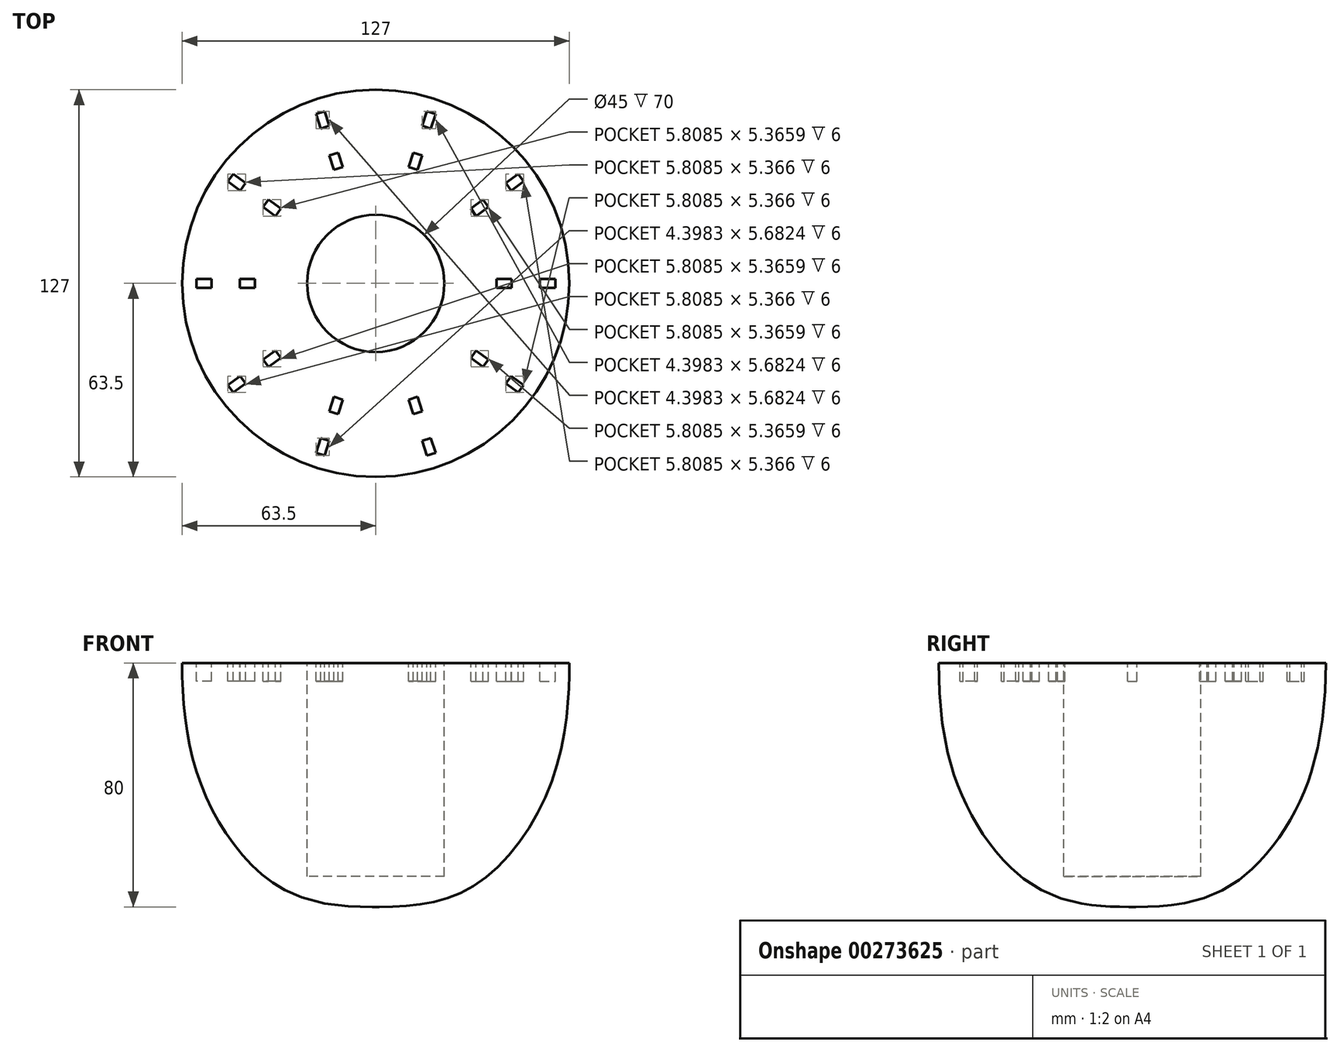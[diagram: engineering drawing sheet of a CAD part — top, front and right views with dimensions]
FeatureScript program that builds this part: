
annotation { "Feature Type Name" : "Feature", "Feature Type Description" : "" }
export const myFeature = defineFeature(function(context is Context, id is Id, definition is map)
    precondition{}
    {
        {
            var Q0;
            Q0=qCreatedBy(makeId("Front.planeOp"),FACE);
            var sketch = newSketch(context, id + "F0", { "sketchPlane" : qUnion([Q0])});
            skLineSegment(sketch, "E0", {"start": v(0, 0) * mm, "end": v(63.5, 0) * mm});
            skLineSegment(sketch, "E1", {"start": v(0, 0) * mm, "end": v(0, -80) * mm});
            skFitSpline(sketch, "E2", {"points": [v(0, -80) * mm, v(31.42, -73.58) * mm, v(58.27, -37.26) * mm, v(63.5, 0) * mm], "startDerivative": vector(100.46, -0.55) * mm, "endDerivative": vector(0, 86.8) * mm});
            skSolve(sketch);
        }
        {
            var Q0;
            Q0 = qSketchRegion(id + "F0", true);
            var Q1;
            Q1=sQuery(id+"F0.wireOp",EDGE,"E1");
            revolve(context, id + "F1", {"entities" : qUnion([Q0]), "axis" : qUnion([Q1]), "revolveType" : RevolveType.FULL});
        }
        {
            var Q0;
            Q0=makeQuery(id+"F1.opRevolve","SWEPT_FACE",FACE,{"disambiguationData":[OSD([sQuery(id+"F0.wireOp",EDGE,"E0")])]});
            var sketch = newSketch(context, id + "F2", { "sketchPlane" : qUnion([Q0])});
            skCircle(sketch, "E3", {"center": v(0, 0) * mm, "radius": 22.5 * mm});
            skSolve(sketch);
        }
        {
            var Q0;
            Q0=makeQuery(id+"F2.imprint","IMPRINT",FACE,{"disambiguationData":[TD([[makeQuery(id+"F2.imprint","IMPRINT",EDGE,{"derivedFrom":sQuery(id+"F2.wireOp",EDGE,"E3")}),1.0]])]});
            extrude(context, id + "F3", {"entities" : qUnion([Q0]), "operationType" : NewBodyOperationType.REMOVE, "oppositeDirection" : true, "depth" : 70 * mm});
        }
        {
            var Q0;
            Q0=qCreatedBy(makeId("Top.planeOp"),FACE);
            var sketch = newSketch(context, id + "F4", { "sketchPlane" : qUnion([Q0])});
            skLineSegment(sketch, "E4.bottom", {"start": v(-39.63, -1.5) * mm, "end": v(-44.63, -1.5) * mm});
            skLineSegment(sketch, "E4.top", {"start": v(-39.63, 1.5) * mm, "end": v(-44.63, 1.5) * mm});
            skLineSegment(sketch, "E4.left", {"start": v(-39.63, -1.5) * mm, "end": v(-39.63, 1.5) * mm});
            skLineSegment(sketch, "E4.right", {"start": v(-44.63, -1.5) * mm, "end": v(-44.63, 1.5) * mm});
            skPoint(sketch, "E4.middle", {"position": v(-42.12, 0) * mm});
            skLineSegment(sketch, "E5.bottom", {"start": v(-53.88, 1.5) * mm, "end": v(-58.88, 1.5) * mm});
            skLineSegment(sketch, "E5.top", {"start": v(-53.88, -1.5) * mm, "end": v(-58.88, -1.5) * mm});
            skLineSegment(sketch, "E5.left", {"start": v(-53.88, 1.5) * mm, "end": v(-53.88, -1.5) * mm});
            skLineSegment(sketch, "E5.right", {"start": v(-58.88, 1.5) * mm, "end": v(-58.88, -1.5) * mm});
            skPoint(sketch, "E5.middle", {"position": v(-56.38, 0) * mm});
            skPoint(sketch, "E6.1.0", {"position": v(-34.08, -24.76) * mm});
            skPoint(sketch, "E6.1.1", {"position": v(-45.6, -33.14) * mm});
            skLineSegment(sketch, "E6.1.2", {"start": v(-42.7, -32.88) * mm, "end": v(-46.75, -35.82) * mm});
            skLineSegment(sketch, "E6.1.3", {"start": v(-44.47, -30.45) * mm, "end": v(-48.51, -33.4) * mm});
            skLineSegment(sketch, "E6.1.4", {"start": v(-32.94, -22.08) * mm, "end": v(-36.98, -25.02) * mm});
            skLineSegment(sketch, "E6.1.5", {"start": v(-31.18, -24.5) * mm, "end": v(-35.22, -27.44) * mm});
            skLineSegment(sketch, "E6.1.6", {"start": v(-44.47, -30.45) * mm, "end": v(-42.7, -32.88) * mm});
            skLineSegment(sketch, "E6.1.7", {"start": v(-35.22, -27.44) * mm, "end": v(-36.98, -25.02) * mm});
            skLineSegment(sketch, "E6.1.8", {"start": v(-31.18, -24.5) * mm, "end": v(-32.94, -22.08) * mm});
            skLineSegment(sketch, "E6.1.9", {"start": v(-48.51, -33.4) * mm, "end": v(-46.75, -35.82) * mm});
            skPoint(sketch, "E6.2.0", {"position": v(-13.02, -40.06) * mm});
            skPoint(sketch, "E6.2.1", {"position": v(-17.42, -53.62) * mm});
            skLineSegment(sketch, "E6.2.2", {"start": v(-15.22, -51.7) * mm, "end": v(-16.77, -56.46) * mm});
            skLineSegment(sketch, "E6.2.3", {"start": v(-18.07, -50.77) * mm, "end": v(-19.62, -55.53) * mm});
            skLineSegment(sketch, "E6.2.4", {"start": v(-13.67, -37.22) * mm, "end": v(-15.22, -41.98) * mm});
            skLineSegment(sketch, "E6.2.5", {"start": v(-10.82, -38.15) * mm, "end": v(-12.36, -42.9) * mm});
            skLineSegment(sketch, "E6.2.6", {"start": v(-18.07, -50.77) * mm, "end": v(-15.22, -51.7) * mm});
            skLineSegment(sketch, "E6.2.7", {"start": v(-12.36, -42.9) * mm, "end": v(-15.22, -41.98) * mm});
            skLineSegment(sketch, "E6.2.8", {"start": v(-10.82, -38.15) * mm, "end": v(-13.67, -37.22) * mm});
            skLineSegment(sketch, "E6.2.9", {"start": v(-19.62, -55.53) * mm, "end": v(-16.77, -56.46) * mm});
            skPoint(sketch, "E6.3.0", {"position": v(13.02, -40.06) * mm});
            skPoint(sketch, "E6.3.1", {"position": v(17.42, -53.62) * mm});
            skLineSegment(sketch, "E6.3.2", {"start": v(18.07, -50.77) * mm, "end": v(19.62, -55.53) * mm});
            skLineSegment(sketch, "E6.3.3", {"start": v(15.22, -51.7) * mm, "end": v(16.77, -56.46) * mm});
            skLineSegment(sketch, "E6.3.4", {"start": v(10.82, -38.15) * mm, "end": v(12.36, -42.9) * mm});
            skLineSegment(sketch, "E6.3.5", {"start": v(13.67, -37.22) * mm, "end": v(15.22, -41.98) * mm});
            skLineSegment(sketch, "E6.3.6", {"start": v(15.22, -51.7) * mm, "end": v(18.07, -50.77) * mm});
            skLineSegment(sketch, "E6.3.7", {"start": v(15.22, -41.98) * mm, "end": v(12.36, -42.9) * mm});
            skLineSegment(sketch, "E6.3.8", {"start": v(13.67, -37.22) * mm, "end": v(10.82, -38.15) * mm});
            skLineSegment(sketch, "E6.3.9", {"start": v(16.77, -56.46) * mm, "end": v(19.62, -55.53) * mm});
            skPoint(sketch, "E6.4.0", {"position": v(34.08, -24.76) * mm});
            skPoint(sketch, "E6.4.1", {"position": v(45.6, -33.14) * mm});
            skLineSegment(sketch, "E6.4.2", {"start": v(44.47, -30.45) * mm, "end": v(48.51, -33.4) * mm});
            skLineSegment(sketch, "E6.4.3", {"start": v(42.7, -32.88) * mm, "end": v(46.75, -35.82) * mm});
            skLineSegment(sketch, "E6.4.4", {"start": v(31.18, -24.5) * mm, "end": v(35.22, -27.44) * mm});
            skLineSegment(sketch, "E6.4.5", {"start": v(32.94, -22.08) * mm, "end": v(36.98, -25.02) * mm});
            skLineSegment(sketch, "E6.4.6", {"start": v(42.7, -32.88) * mm, "end": v(44.47, -30.45) * mm});
            skLineSegment(sketch, "E6.4.7", {"start": v(36.98, -25.02) * mm, "end": v(35.22, -27.44) * mm});
            skLineSegment(sketch, "E6.4.8", {"start": v(32.94, -22.08) * mm, "end": v(31.18, -24.5) * mm});
            skLineSegment(sketch, "E6.4.9", {"start": v(46.75, -35.82) * mm, "end": v(48.51, -33.4) * mm});
            skPoint(sketch, "E6.5.0", {"position": v(42.12, 0) * mm});
            skPoint(sketch, "E6.5.1", {"position": v(56.38, 0) * mm});
            skLineSegment(sketch, "E6.5.2", {"start": v(53.88, 1.5) * mm, "end": v(58.88, 1.5) * mm});
            skLineSegment(sketch, "E6.5.3", {"start": v(53.88, -1.5) * mm, "end": v(58.88, -1.5) * mm});
            skLineSegment(sketch, "E6.5.4", {"start": v(39.63, -1.5) * mm, "end": v(44.63, -1.5) * mm});
            skLineSegment(sketch, "E6.5.5", {"start": v(39.63, 1.5) * mm, "end": v(44.63, 1.5) * mm});
            skLineSegment(sketch, "E6.5.6", {"start": v(53.88, -1.5) * mm, "end": v(53.88, 1.5) * mm});
            skLineSegment(sketch, "E6.5.7", {"start": v(44.63, 1.5) * mm, "end": v(44.63, -1.5) * mm});
            skLineSegment(sketch, "E6.5.8", {"start": v(39.63, 1.5) * mm, "end": v(39.63, -1.5) * mm});
            skLineSegment(sketch, "E6.5.9", {"start": v(58.88, -1.5) * mm, "end": v(58.88, 1.5) * mm});
            skPoint(sketch, "E6.6.0", {"position": v(34.08, 24.76) * mm});
            skPoint(sketch, "E6.6.1", {"position": v(45.6, 33.14) * mm});
            skLineSegment(sketch, "E6.6.2", {"start": v(42.7, 32.88) * mm, "end": v(46.75, 35.82) * mm});
            skLineSegment(sketch, "E6.6.3", {"start": v(44.47, 30.45) * mm, "end": v(48.51, 33.4) * mm});
            skLineSegment(sketch, "E6.6.4", {"start": v(32.94, 22.08) * mm, "end": v(36.98, 25.02) * mm});
            skLineSegment(sketch, "E6.6.5", {"start": v(31.18, 24.5) * mm, "end": v(35.22, 27.44) * mm});
            skLineSegment(sketch, "E6.6.6", {"start": v(44.47, 30.45) * mm, "end": v(42.7, 32.88) * mm});
            skLineSegment(sketch, "E6.6.7", {"start": v(35.22, 27.44) * mm, "end": v(36.98, 25.02) * mm});
            skLineSegment(sketch, "E6.6.8", {"start": v(31.18, 24.5) * mm, "end": v(32.94, 22.08) * mm});
            skLineSegment(sketch, "E6.6.9", {"start": v(48.51, 33.4) * mm, "end": v(46.75, 35.82) * mm});
            skPoint(sketch, "E6.7.0", {"position": v(13.02, 40.06) * mm});
            skPoint(sketch, "E6.7.1", {"position": v(17.42, 53.62) * mm});
            skLineSegment(sketch, "E6.7.2", {"start": v(15.22, 51.7) * mm, "end": v(16.77, 56.46) * mm});
            skLineSegment(sketch, "E6.7.3", {"start": v(18.07, 50.77) * mm, "end": v(19.62, 55.53) * mm});
            skLineSegment(sketch, "E6.7.4", {"start": v(13.67, 37.22) * mm, "end": v(15.22, 41.98) * mm});
            skLineSegment(sketch, "E6.7.5", {"start": v(10.82, 38.15) * mm, "end": v(12.36, 42.9) * mm});
            skLineSegment(sketch, "E6.7.6", {"start": v(18.07, 50.77) * mm, "end": v(15.22, 51.7) * mm});
            skLineSegment(sketch, "E6.7.7", {"start": v(12.36, 42.9) * mm, "end": v(15.22, 41.98) * mm});
            skLineSegment(sketch, "E6.7.8", {"start": v(10.82, 38.15) * mm, "end": v(13.67, 37.22) * mm});
            skLineSegment(sketch, "E6.7.9", {"start": v(19.62, 55.53) * mm, "end": v(16.77, 56.46) * mm});
            skPoint(sketch, "E6.8.0", {"position": v(-13.02, 40.06) * mm});
            skPoint(sketch, "E6.8.1", {"position": v(-17.42, 53.62) * mm});
            skLineSegment(sketch, "E6.8.2", {"start": v(-18.07, 50.77) * mm, "end": v(-19.62, 55.53) * mm});
            skLineSegment(sketch, "E6.8.3", {"start": v(-15.22, 51.7) * mm, "end": v(-16.77, 56.46) * mm});
            skLineSegment(sketch, "E6.8.4", {"start": v(-10.82, 38.15) * mm, "end": v(-12.36, 42.9) * mm});
            skLineSegment(sketch, "E6.8.5", {"start": v(-13.67, 37.22) * mm, "end": v(-15.22, 41.98) * mm});
            skLineSegment(sketch, "E6.8.6", {"start": v(-15.22, 51.7) * mm, "end": v(-18.07, 50.77) * mm});
            skLineSegment(sketch, "E6.8.7", {"start": v(-15.22, 41.98) * mm, "end": v(-12.36, 42.9) * mm});
            skLineSegment(sketch, "E6.8.8", {"start": v(-13.67, 37.22) * mm, "end": v(-10.82, 38.15) * mm});
            skLineSegment(sketch, "E6.8.9", {"start": v(-16.77, 56.46) * mm, "end": v(-19.62, 55.53) * mm});
            skPoint(sketch, "E6.9.0", {"position": v(-34.08, 24.76) * mm});
            skPoint(sketch, "E6.9.1", {"position": v(-45.6, 33.14) * mm});
            skLineSegment(sketch, "E6.9.2", {"start": v(-44.47, 30.45) * mm, "end": v(-48.51, 33.4) * mm});
            skLineSegment(sketch, "E6.9.3", {"start": v(-42.7, 32.88) * mm, "end": v(-46.75, 35.82) * mm});
            skLineSegment(sketch, "E6.9.4", {"start": v(-31.18, 24.5) * mm, "end": v(-35.22, 27.44) * mm});
            skLineSegment(sketch, "E6.9.5", {"start": v(-32.94, 22.08) * mm, "end": v(-36.98, 25.02) * mm});
            skLineSegment(sketch, "E6.9.6", {"start": v(-42.7, 32.88) * mm, "end": v(-44.47, 30.45) * mm});
            skLineSegment(sketch, "E6.9.7", {"start": v(-36.98, 25.02) * mm, "end": v(-35.22, 27.44) * mm});
            skLineSegment(sketch, "E6.9.8", {"start": v(-32.94, 22.08) * mm, "end": v(-31.18, 24.5) * mm});
            skLineSegment(sketch, "E6.9.9", {"start": v(-46.75, 35.82) * mm, "end": v(-48.51, 33.4) * mm});
            skPoint(sketch, "E6.center", {"position": v(0, 0) * mm});
            skSolve(sketch);
        }
        {
            var Q0;
            Q0 = qSketchRegion(id + "F4", true);
            extrude(context, id + "F5", {"entities" : qUnion([Q0]), "operationType" : NewBodyOperationType.REMOVE, "oppositeDirection" : true, "depth" : 6 * mm});
        }
    });
